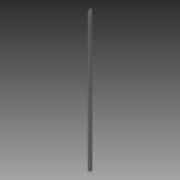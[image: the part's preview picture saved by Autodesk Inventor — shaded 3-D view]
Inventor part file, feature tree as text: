
AUTODESK INVENTOR PART (.ipt)
format: ipt  version: 2015 SP1 (Build 190203100, 203)  size: 124,928 bytes
history: native  units: mm
features: extrude x4, sketch x4
ambient origin geometry x8: Origin, YZ Plane, XZ Plane, XY Plane, X Axis, Y Axis, Z Axis, Center Point
bodies: Solid1 (feature_tree)
feature tree (8):
  extrude  "Extrusion1"  Depth=50.0mm
  extrude  "Extrusion2"  Depth=3.0mm
  extrude  "Extrusion3"  Depth=8.37758mm
  extrude  "Extrusion4"  Depth=10.0mm
  sketch  "Sketch1"  dims[d0=50.0mm d1=50.0mm]
  sketch  "Sketch2"  dims[d2=3.0mm d3=3.0mm]
  sketch  "Sketch3"  dims[d4=2905.0mm d5=0.0mm d6=8.37758mm]
  sketch  "Sketch4"  dims[d7=2100.0mm d8=0.0mm d9=20.0mm d10=750.0mm d11=10.0mm d12=0.0mm d13=7.0mm d14=25.0mm d15=12.5mm d16=25.0mm d17=1405.0mm d18=1405.0mm d19=0.0mm d20=0.0mm]
